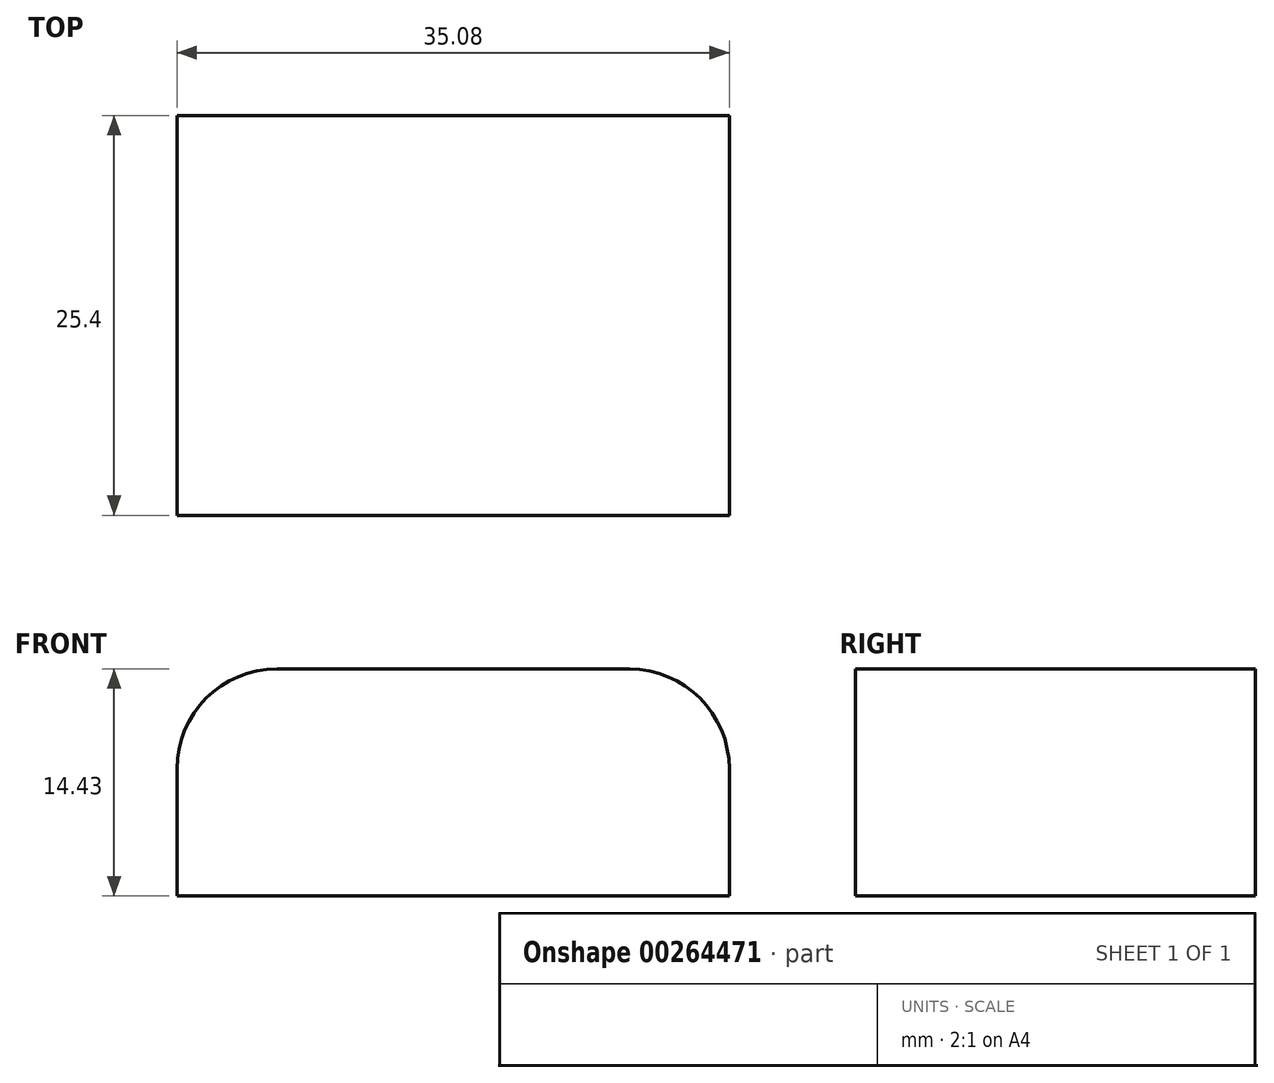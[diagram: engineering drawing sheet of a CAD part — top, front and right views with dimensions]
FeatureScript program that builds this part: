
annotation { "Feature Type Name" : "Feature", "Feature Type Description" : "" }
export const myFeature = defineFeature(function(context is Context, id is Id, definition is map)
    precondition{}
    {
        {
            var Q0;
            Q0=qCreatedBy(makeId("Front.planeOp"),FACE);
            var sketch = newSketch(context, id + "F0", { "sketchPlane" : qUnion([Q0])});
            skLineSegment(sketch, "E0.bottom", {"start": v(-19.72, 0) * mm, "end": v(15.36, 0) * mm});
            skLineSegment(sketch, "E0.top", {"start": v(-13.37, 14.43) * mm, "end": v(9, 14.43) * mm});
            skLineSegment(sketch, "E0.left", {"start": v(-19.72, 0) * mm, "end": v(-19.72, 8.08) * mm});
            skLineSegment(sketch, "E0.right", {"start": v(15.36, 0) * mm, "end": v(15.36, 8.08) * mm});
            skPoint(sketch, "E1.visualSharp", {"position": v(-19.72, 14.43) * mm});
            skArc(sketch, "E1.filletArc", {"start": v(-13.37, 14.43) * mm, "mid": v(-17.86, 12.57) * mm, "end": v(-19.72, 8.08) * mm});
            skPoint(sketch, "E2.visualSharp", {"position": v(15.36, 14.43) * mm});
            skArc(sketch, "E2.filletArc", {"start": v(15.36, 8.08) * mm, "mid": v(13.5, 12.57) * mm, "end": v(9, 14.43) * mm});
            skSolve(sketch);
        }
        {
            var Q0;
            Q0 = qSketchRegion(id + "F0", true);
            extrude(context, id + "F1", {"entities" : qUnion([Q0]), "oppositeDirection" : true, "depth" : 25.4 * mm});
        }
    });
